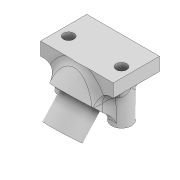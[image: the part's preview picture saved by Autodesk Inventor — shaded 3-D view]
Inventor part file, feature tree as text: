
AUTODESK INVENTOR PART (.ipt)
format: ipt  version: 2022 (Build 260153000, 153)  size: 540,160 bytes
history: native  units: mm
features: extrude x9, sketch x6, plane x2, fillet x2, projected_geometry x2
ambient origin geometry x8: Origin, YZ Plane, XZ Plane, XY Plane, X Axis, Y Axis, Z Axis, Center Point
bodies: Body1 (feature_tree)
feature tree (21):
  sketch  "Sketch6"  dims[d29=22.0mm d30=14.0mm]
  extrude  "Extrusion6"  Depth=14.0mm
  plane  "Work Plane3"
  extrude  "Extrusion7"  [1 undecoded]
  extrude  "Extrusion9"  Depth=5.0mm
  plane  "Work Plane4"
  extrude  "Extrusion25"  Depth=9.8mm
  extrude  "Extrusion19"  Depth=3.2mm
  extrude  "Extrusion20"  Depth=5.5mm
  extrude  "Extrusion22"  Depth=5.5mm
  extrude  "Extrusion23"  Depth=3.0mm
  extrude  "Extrusion26"  Depth=3.0mm
  fillet  "Fillet10"  Radius=10.0mm
  fillet  "Fillet11"  Radius=20.0mm
  sketch  "Sketch7"  dims[d31=4.0mm d32=0.0mm d33=-7.330383mm]
  sketch  "Sketch9"  dims[d34=3.0mm d35=5.0mm]
  projected_geometry  "Projected Loop8"
  sketch  "Sketch22"  dims[d36=11.0mm d37=9.8mm]
  sketch  "Sketch26"  dims[d38=12.0mm d39=0.0mm d43=3.2mm]
  projected_geometry  "Projected Loop11"
  sketch  "Sketch27"  dims[d44=3.2mm d45=5.5mm d46=5.5mm d47=3.0mm d48=3.0mm d49=10.0mm d50=0.0mm d51=20.0mm d52=0.0mm d66=-12.0mm d87=12.2mm d88=15.0mm d89=8.0mm d90=0.0mm d91=4.0mm d92=20.0mm d93=0.0mm d94=0.0mm d97=100.0mm d98=0.0mm d99=100.0mm d100=0.0mm d105=6.0mm d106=6.0mm d107=10.0mm d108=0.0mm d109=100.0mm d110=0.0mm d116=3.0mm d117=2.0mm d12=0.5mm d13=0.872665mm d14=0.5mm d15=0.872665mm d84=0.5mm d85=0.872665mm d86=0.5mm d112=0.5mm d113=0.872665mm d114=0.5mm d115=0.872665mm]
note: 1 required parameter value undecoded (feature->parameter linkage not recoverable at this tier; creation-order binding heuristic only, values carry confidence <= 0.55)
